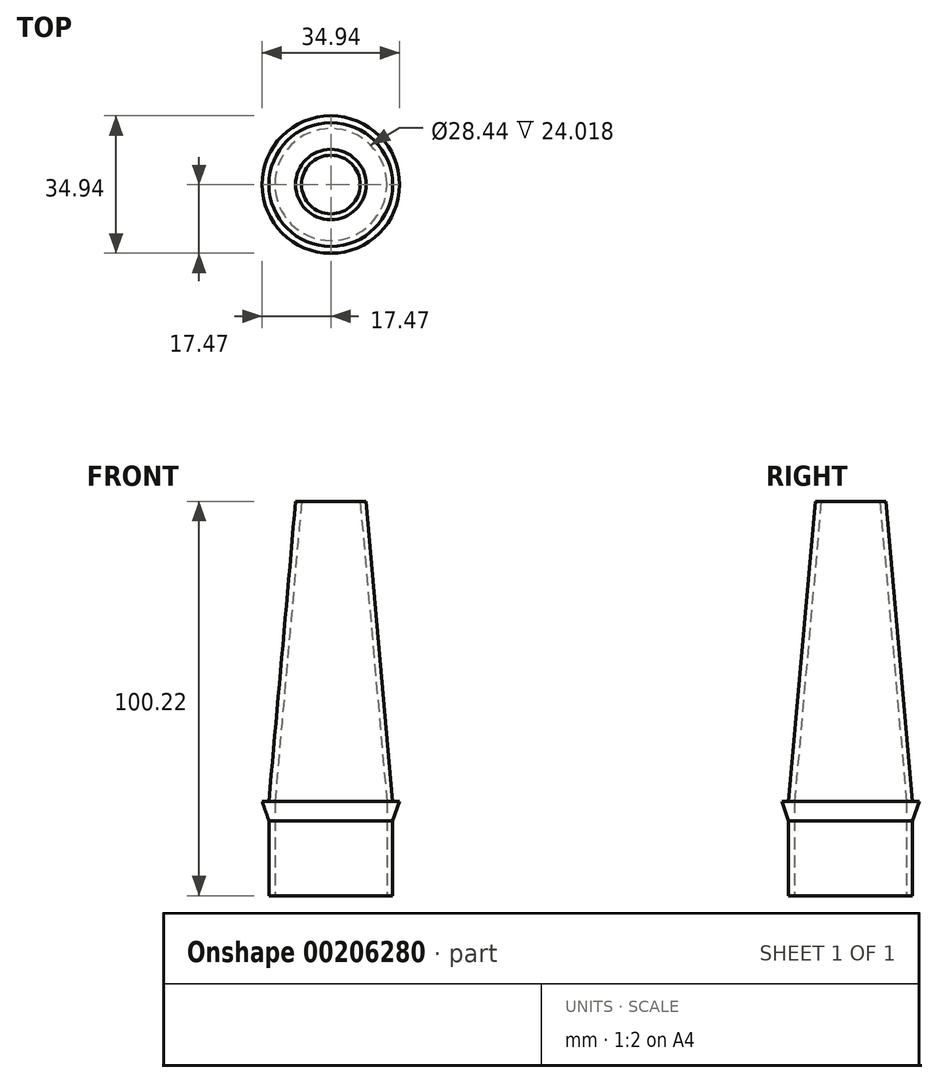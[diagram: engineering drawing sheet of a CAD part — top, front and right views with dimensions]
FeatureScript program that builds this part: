
annotation { "Feature Type Name" : "Feature", "Feature Type Description" : "" }
export const myFeature = defineFeature(function(context is Context, id is Id, definition is map)
    precondition{}
    {
        {
            var Q0;
            Q0=qCreatedBy(makeId("Top.planeOp"),FACE);
            var sketch = newSketch(context, id + "F0", { "sketchPlane" : qUnion([Q0])});
            skCircle(sketch, "E0", {"center": v(0, 0) * mm, "radius": 15.75 * mm});
            skCircle(sketch, "E1", {"center": v(0, 0) * mm, "radius": 14.25 * mm});
            skSolve(sketch);
        }
        {
            var Q0;
            Q0=qCreatedBy(makeId("Right.planeOp"),FACE);
            var sketch = newSketch(context, id + "F1", { "sketchPlane" : qUnion([Q0])});
            skLineSegment(sketch, "E2.bottom", {"start": v(-14.22, 24.02) * mm, "end": v(-17.47, 24.02) * mm});
            skLineSegment(sketch, "E2.top", {"start": v(-14.22, 19.02) * mm, "end": v(-15.72, 19.02) * mm});
            skLineSegment(sketch, "E2.left", {"start": v(-14.22, 24.02) * mm, "end": v(-14.22, 19.02) * mm});
            skLineSegment(sketch, "E3", {"start": v(-15.72, 19.02) * mm, "end": v(-17.47, 24.02) * mm});
            skLineSegment(sketch, "E4", {"start": v(-15.72, 19.02) * mm, "end": v(-15.72, 0) * mm});
            skLineSegment(sketch, "E5", {"start": v(-15.72, 0) * mm, "end": v(-14.22, 0) * mm});
            skLineSegment(sketch, "E6", {"start": v(-14.22, 0) * mm, "end": v(-14.22, 19.02) * mm});
            skLineSegment(sketch, "E7", {"start": v(-15.72, 24.02) * mm, "end": v(-8.95, 100.22) * mm});
            skLineSegment(sketch, "E8", {"start": v(-8.95, 100.22) * mm, "end": v(-7.46, 100.09) * mm});
            skLineSegment(sketch, "E9", {"start": v(-7.46, 100.09) * mm, "end": v(-14.22, 24.02) * mm});
            skSolve(sketch);
        }
        {
            var Q0;
            Q0 = qSketchRegion(id + "F1", true);
            var Q1;
            Q1=sQuery(id+"F0.wireOp",EDGE,"E1");
            revolve(context, id + "F2", {"entities" : qUnion([Q0]), "axis" : qUnion([Q1]), "revolveType" : RevolveType.FULL});
        }
    });
